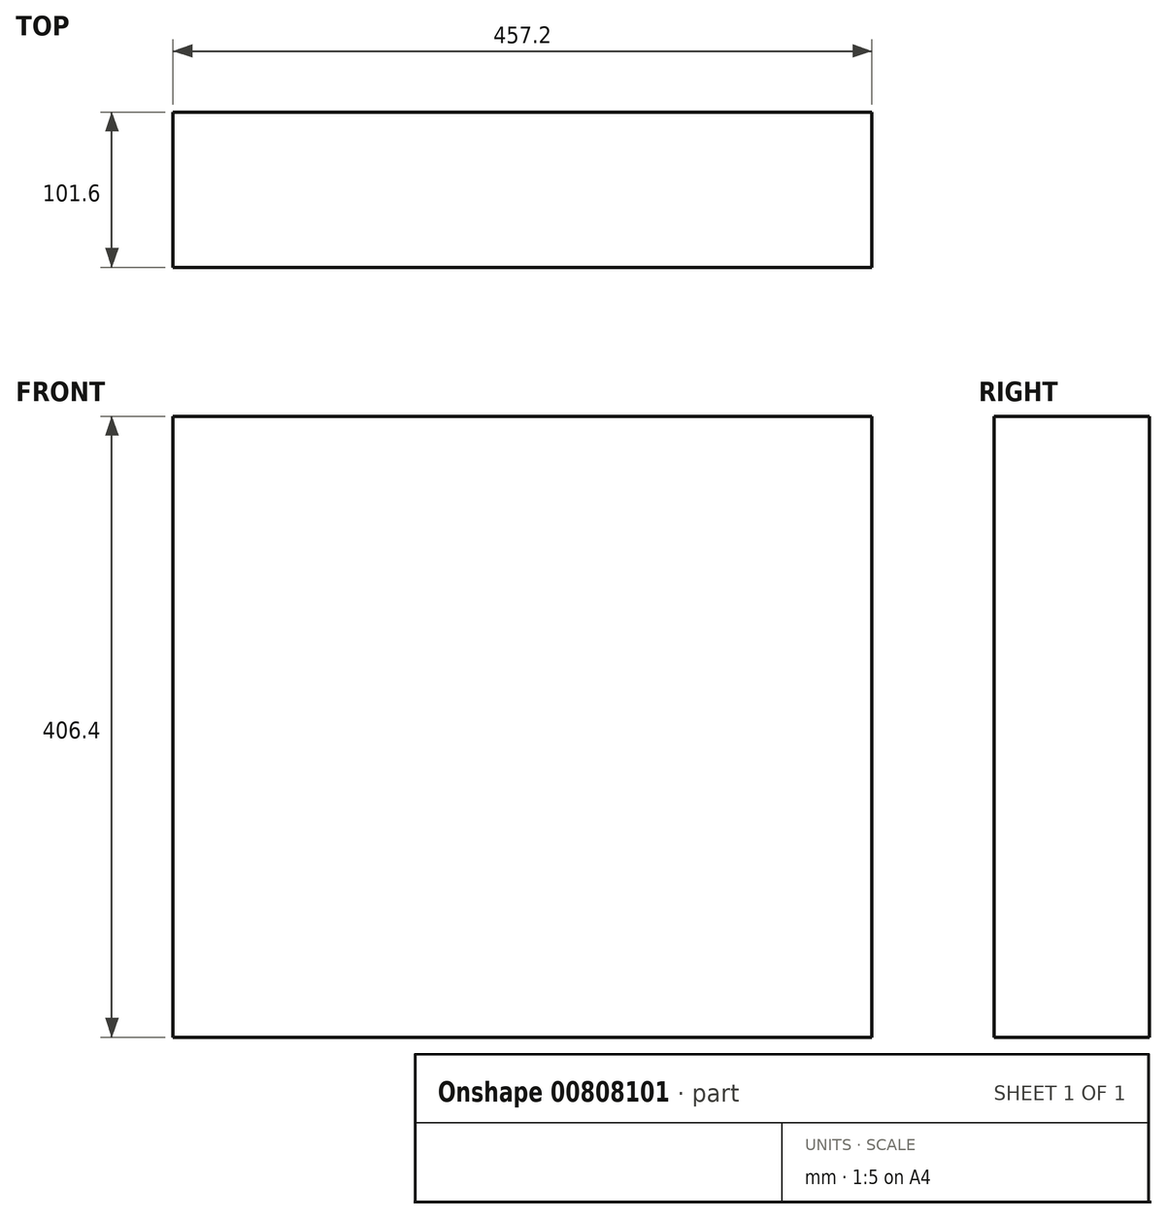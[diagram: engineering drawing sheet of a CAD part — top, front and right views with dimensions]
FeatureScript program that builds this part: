
annotation { "Feature Type Name" : "Feature", "Feature Type Description" : "" }
export const myFeature = defineFeature(function(context is Context, id is Id, definition is map)
    precondition{}
    {
        {
            var Q0;
            Q0=qCreatedBy(makeId("Front.planeOp"),FACE);
            var sketch = newSketch(context, id + "F0", { "sketchPlane" : qUnion([Q0])});
            skLineSegment(sketch, "E0.bottom", {"start": v(228.6, 203.2) * mm, "end": v(-228.6, 203.2) * mm});
            skLineSegment(sketch, "E0.top", {"start": v(228.6, -203.2) * mm, "end": v(-228.6, -203.2) * mm});
            skLineSegment(sketch, "E0.left", {"start": v(228.6, 203.2) * mm, "end": v(228.6, -203.2) * mm});
            skLineSegment(sketch, "E0.right", {"start": v(-228.6, 203.2) * mm, "end": v(-228.6, -203.2) * mm});
            skPoint(sketch, "E0.middle", {"position": v(0, 0) * mm});
            skSolve(sketch);
        }
        {
            var Q0;
            Q0=qSketchRegion(id+"F0",true);
            extrude(context, id + "F1", {"entities" : qUnion([Q0]), "depth" : 101.6 * mm, "offsetDistance" : 25.4 * mm});
        }
    });
